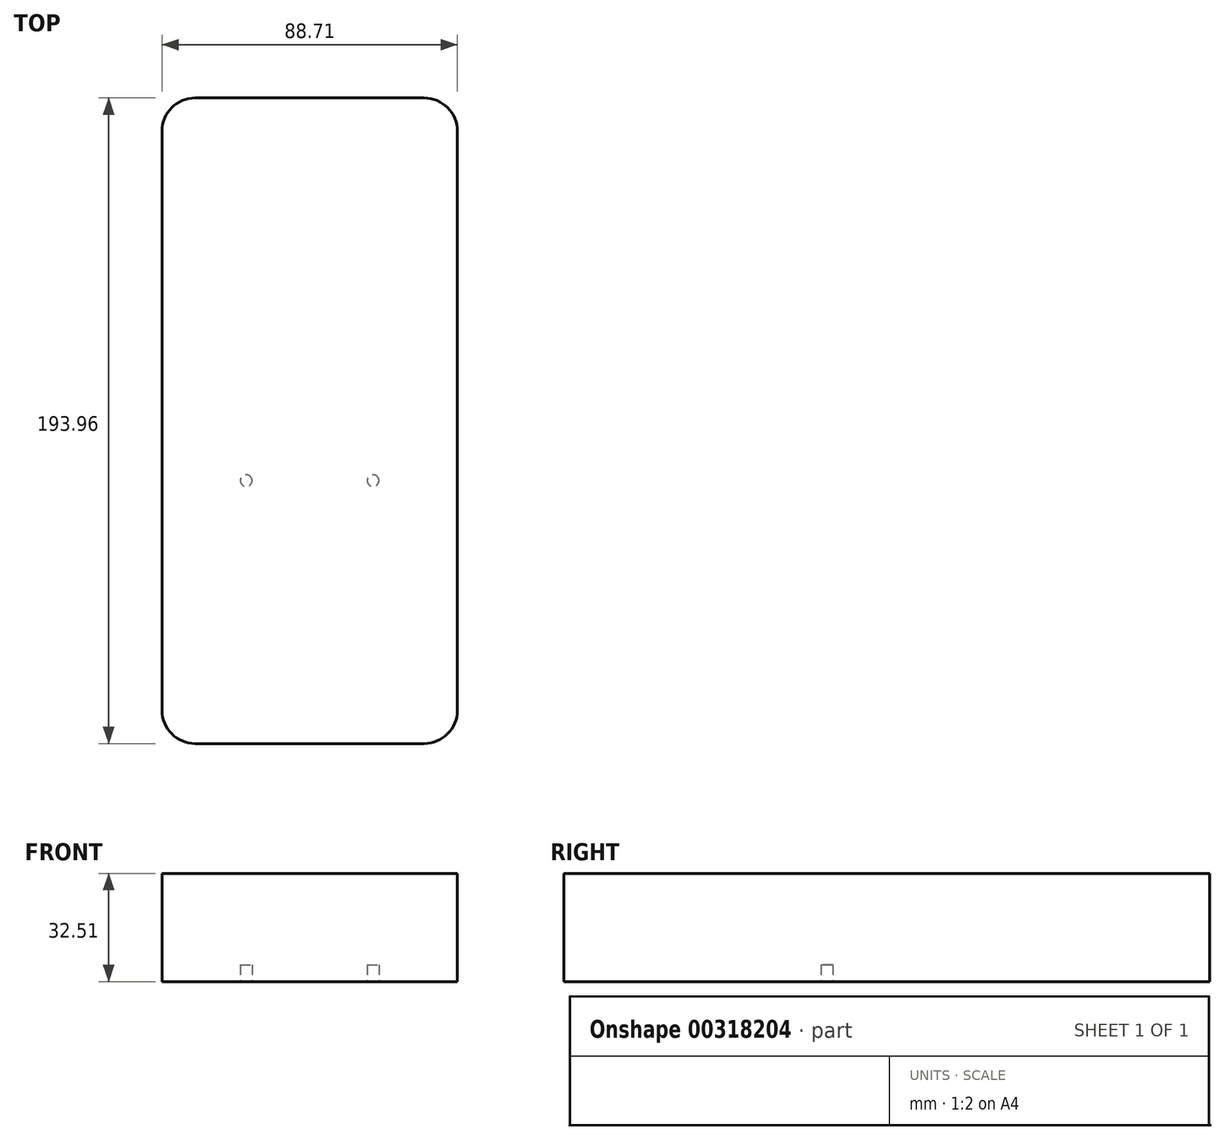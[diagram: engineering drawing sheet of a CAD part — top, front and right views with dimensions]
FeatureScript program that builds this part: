
annotation { "Feature Type Name" : "Feature", "Feature Type Description" : "" }
export const myFeature = defineFeature(function(context is Context, id is Id, definition is map)
    precondition{}
    {
        {
            var Q0;
            Q0=qCreatedBy(makeId("Top.planeOp"),FACE);
            var sketch = newSketch(context, id + "F0", { "sketchPlane" : qUnion([Q0])});
            skLineSegment(sketch, "E0.bottom", {"start": v(10, 0) * mm, "end": v(78.71, 0) * mm});
            skLineSegment(sketch, "E0.top", {"start": v(10, -193.96) * mm, "end": v(78.71, -193.96) * mm});
            skLineSegment(sketch, "E0.left", {"start": v(0, -10) * mm, "end": v(0, -183.96) * mm});
            skLineSegment(sketch, "E0.right", {"start": v(88.7, -10) * mm, "end": v(88.71, -183.96) * mm});
            skPoint(sketch, "E1.visualSharp", {"position": v(0, 0) * mm});
            skArc(sketch, "E1.filletArc", {"start": v(10, 0) * mm, "mid": v(2.93, -2.93) * mm, "end": v(0, -10) * mm});
            skPoint(sketch, "E2.visualSharp", {"position": v(88.7, 0) * mm});
            skArc(sketch, "E2.filletArc", {"start": v(88.7, -10) * mm, "mid": v(85.78, -2.93) * mm, "end": v(78.71, 0) * mm});
            skPoint(sketch, "E3.visualSharp", {"position": v(0, -193.96) * mm});
            skArc(sketch, "E3.filletArc", {"start": v(0, -183.96) * mm, "mid": v(2.93, -191.03) * mm, "end": v(10, -193.96) * mm});
            skPoint(sketch, "E4.visualSharp", {"position": v(88.71, -193.96) * mm});
            skArc(sketch, "E4.filletArc", {"start": v(78.71, -193.96) * mm, "mid": v(85.78, -191.03) * mm, "end": v(88.7, -183.96) * mm});
            skSolve(sketch);
        }
        {
            var Q0;
            Q0=makeQuery(id+"F0.imprint","IMPRINT",FACE,{"disambiguationData":[TD([[makeQuery(id+"F0.imprint","IMPRINT",EDGE,{"derivedFrom":sQuery(id+"F0.wireOp",EDGE,"E0.bottom")}),-1.0]])]});
            extrude(context, id + "F1", {"entities" : qUnion([Q0]), "depth" : 32.5 * mm});
        }
        {
            var Q0;
            Q0=makeQuery(id+"F1.opExtrude","CAP_FACE",FACE,{"disambiguationData":[OSD([sQuery(id+"F0.wireOp",EDGE,"E0.bottom"),sQuery(id+"F0.wireOp",EDGE,"E0.top"),sQuery(id+"F0.wireOp",EDGE,"E0.left"),sQuery(id+"F0.wireOp",EDGE,"E0.right"),sQuery(id+"F0.wireOp",EDGE,"E1.filletArc"),sQuery(id+"F0.wireOp",EDGE,"E2.filletArc"),sQuery(id+"F0.wireOp",EDGE,"E3.filletArc"),sQuery(id+"F0.wireOp",EDGE,"E4.filletArc")])],"isStart":true});
            var sketch = newSketch(context, id + "F2", { "sketchPlane" : qUnion([Q0])});
            skLineSegment(sketch, "E5", {"start": v(88.7, 114.98) * mm, "end": v(0, 114.98) * mm, "construction": true});
            skLineSegment(sketch, "E6", {"start": v(63.4, 193.96) * mm, "end": v(63.4, 114.98) * mm, "construction": true});
            skLineSegment(sketch, "E7", {"start": v(25.3, 193.96) * mm, "end": v(25.3, 114.98) * mm, "construction": true});
            skCircle(sketch, "E8", {"center": v(63.4, 114.98) * mm, "radius": 1.75 * mm});
            skCircle(sketch, "E9", {"center": v(25.3, 114.98) * mm, "radius": 1.75 * mm});
            skSolve(sketch);
        }
        {
            var Q0;
            Q0=makeQuery(id+"F2.imprint","IMPRINT",FACE,{"disambiguationData":[TD([[makeQuery(id+"F2.imprint","IMPRINT",EDGE,{"derivedFrom":sQuery(id+"F2.wireOp",EDGE,"E8")}),1.0]])]});
            var Q1;
            Q1=makeQuery(id+"F2.imprint","IMPRINT",FACE,{"disambiguationData":[TD([[makeQuery(id+"F2.imprint","IMPRINT",EDGE,{"derivedFrom":sQuery(id+"F2.wireOp",EDGE,"E9")}),1.0]])]});
            extrude(context, id + "F3", {"entities" : qUnion([Q0, Q1]), "operationType" : NewBodyOperationType.REMOVE, "oppositeDirection" : true, "depth" : 5 * mm});
        }
    });
